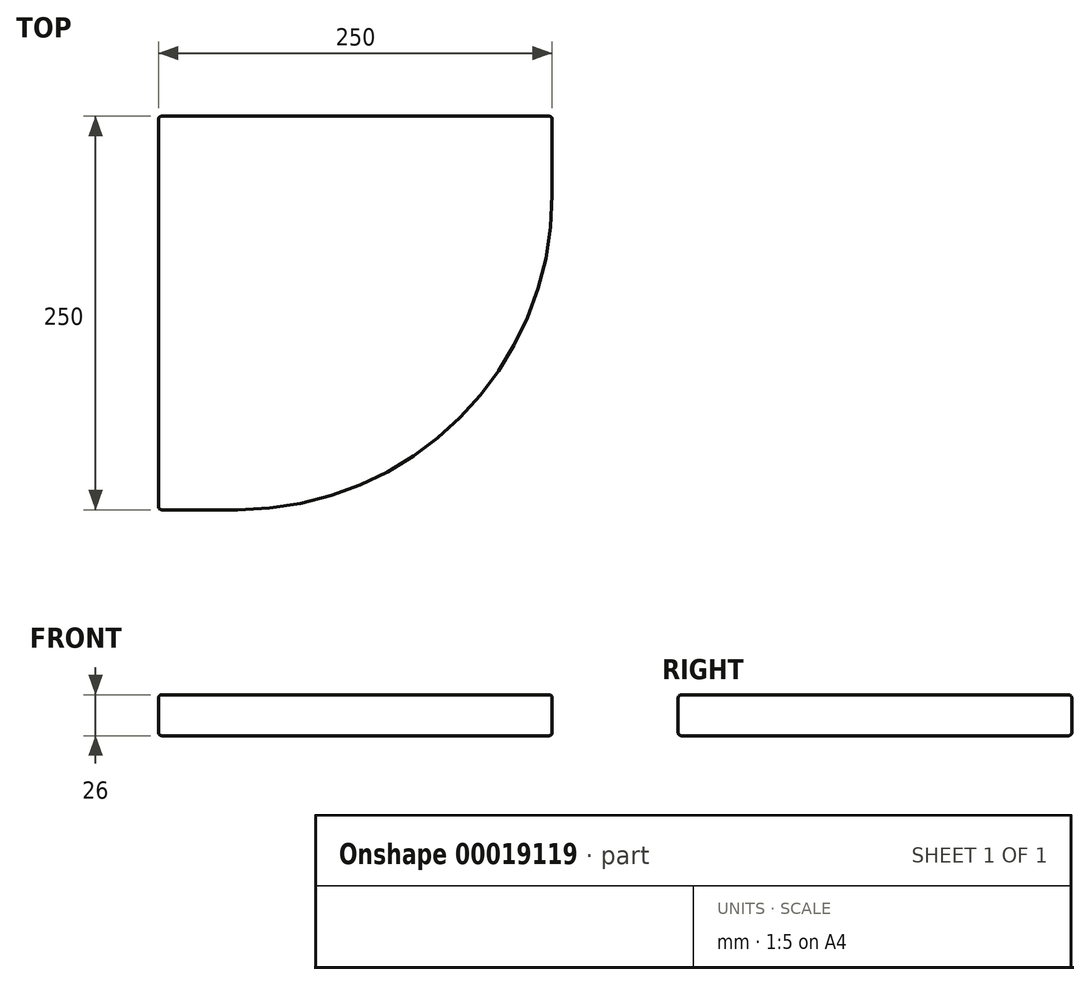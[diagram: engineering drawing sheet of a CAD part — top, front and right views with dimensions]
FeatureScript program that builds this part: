
annotation { "Feature Type Name" : "Feature", "Feature Type Description" : "" }
export const myFeature = defineFeature(function(context is Context, id is Id, definition is map)
    precondition{}
    {
        {
            var Q0;
            Q0=qCreatedBy(makeId("Top.planeOp"),FACE);
            var sketch = newSketch(context, id + "F0", { "sketchPlane" : qUnion([Q0])});
            skLineSegment(sketch, "E0", {"start": v(0, 0) * mm, "end": v(0, -250) * mm});
            skLineSegment(sketch, "E1", {"start": v(250, 0) * mm, "end": v(0, 0) * mm});
            skLineSegment(sketch, "E2", {"start": v(0, -250) * mm, "end": v(50, -250) * mm});
            skLineSegment(sketch, "E3", {"start": v(250, 0) * mm, "end": v(250, -50) * mm});
            skArc(sketch, "E4", {"start": v(50, -250) * mm, "mid": v(191.42, -191.42) * mm, "end": v(250, -50) * mm});
            skSolve(sketch);
        }
        {
            var Q0;
            Q0=makeQuery(id+"F0.imprint","IMPRINT",FACE,{"disambiguationData":[TD([[makeQuery(id+"F0.imprint","IMPRINT",EDGE,{"derivedFrom":sQuery(id+"F0.wireOp",EDGE,"E0")}),1.0]])]});
            extrude(context, id + "F1", {"entities" : qUnion([Q0]), "depth" : 26 * mm});
        }
        {
            var Q0;
            Q0=makeQuery(id+"F1.opExtrude","CAP_FACE",FACE,{"disambiguationData":[OSD([sQuery(id+"F0.wireOp",EDGE,"E0"),sQuery(id+"F0.wireOp",EDGE,"E1"),sQuery(id+"F0.wireOp",EDGE,"E2"),sQuery(id+"F0.wireOp",EDGE,"E3"),sQuery(id+"F0.wireOp",EDGE,"E4")])],"isStart":false});
            var Q1;
            Q1=makeQuery(id+"F1.opExtrude","CAP_EDGE",EDGE,{"disambiguationData":[OSD([sQuery(id+"F0.wireOp",EDGE,"E0")])],"isStart":true});
            var Q2;
            Q2=makeQuery(id+"F1.opExtrude","CAP_EDGE",EDGE,{"disambiguationData":[OSD([sQuery(id+"F0.wireOp",EDGE,"E2")])],"isStart":true});
            var Q3;
            Q3=makeQuery(id+"F1.opExtrude","CAP_EDGE",EDGE,{"disambiguationData":[OSD([sQuery(id+"F0.wireOp",EDGE,"E4")])],"isStart":true});
            var Q4;
            Q4=makeQuery(id+"F1.opExtrude","CAP_EDGE",EDGE,{"disambiguationData":[OSD([sQuery(id+"F0.wireOp",EDGE,"E3")])],"isStart":true});
            var Q5;
            Q5=makeQuery(id+"F1.opExtrude","CAP_EDGE",EDGE,{"disambiguationData":[OSD([sQuery(id+"F0.wireOp",EDGE,"E1")])],"isStart":true});
            var Q6;
            Q6=makeQuery(id+"F1.opExtrude","SWEPT_EDGE",EDGE,{"disambiguationData":[OSD([sQuery(id+"F0.wireOp",EDGE,"E0"),sQuery(id+"F0.wireOp",EDGE,"E2")])]});
            var Q7;
            Q7=makeQuery(id+"F1.opExtrude","SWEPT_EDGE",EDGE,{"disambiguationData":[OSD([sQuery(id+"F0.wireOp",EDGE,"E1"),sQuery(id+"F0.wireOp",EDGE,"E3")])]});
            var Q8;
            Q8=makeQuery(id+"F1.opExtrude","SWEPT_EDGE",EDGE,{"disambiguationData":[OSD([sQuery(id+"F0.wireOp",EDGE,"E0"),sQuery(id+"F0.wireOp",EDGE,"E1")])]});
            fillet(context, id + "F2", {"entities" : qUnion([Q0, Q1, Q2, Q3, Q4, Q5, Q6, Q7, Q8]), "radius" : 2 * mm, "tangentPropagation" : true, "allowEdgeOverflow" : false});
        }
    });
